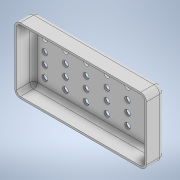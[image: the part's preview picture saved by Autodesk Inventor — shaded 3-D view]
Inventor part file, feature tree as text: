
AUTODESK INVENTOR PART (.ipt)
format: ipt  version: 2021 (Build 250183000, 183)  size: 185,856 bytes
history: native  units: mm
features: extrude x2, fillet x2, sketch x2, other x1, shell x1, pattern_linear x1
ambient origin geometry x8: Origin, YZ Plane, XZ Plane, XY Plane, X Axis, Y Axis, Z Axis, Center Point
bodies: Body1 (feature_tree)
feature tree (9):
  other  "Sólido1"
  extrude  "Extrusão1"  Depth=35.0mm
  fillet  "Arredondamento1"  Radius=10.0mm
  fillet  "Arredondamento2"  Radius=3.0mm
  shell  "Casca1"  Thickness=3.0mm
  extrude  "Extrusão2"  Depth=3.0mm
  pattern_linear  "Padrão retangular1"  Spacing1=4.0mm  [1 undecoded]
  sketch  "Esboço1"  dims[d0=70.0mm d1=35.0mm d2=10.0mm d3=0.0mm d4=3.0mm d5=3.0mm]
  sketch  "Esboço2"  dims[d6=1.0mm d7=3.0mm d8=4.0mm d9=4.0mm d10=0.0mm d11=0.0mm d12=60.0mm d14=11.0mm d15=40.0mm d17=6.0mm]
note: 1 required parameter value undecoded (feature->parameter linkage not recoverable at this tier; creation-order binding heuristic only, values carry confidence <= 0.55)
